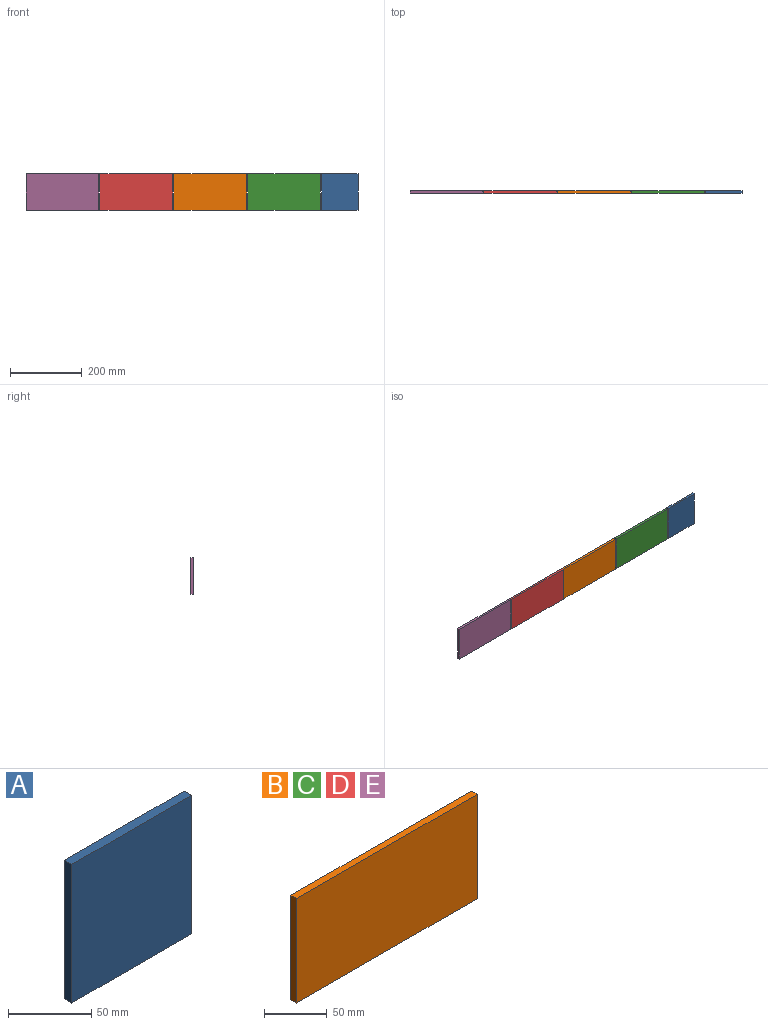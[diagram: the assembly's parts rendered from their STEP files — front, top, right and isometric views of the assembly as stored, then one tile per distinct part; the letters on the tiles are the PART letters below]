
ASSEMBLY  parts=5 mates=1
PART A: 6 faces, bbox 101.6x6.4x101.6 mm
  f0: plane 101.6x6.35mm, normal (-1,0,0), area 645.2mm2, adj f1,f3,f4,f5
  f1: plane 101.6x6.35mm, normal (0,0,-1), area 645.2mm2, adj f0,f2,f4,f5
  f2: plane 101.6x6.35mm, normal (1,0,0), area 645.2mm2, adj f1,f3,f4,f5
  f3: plane 101.6x6.35mm, normal (0,0,1), area 645.2mm2, adj f0,f2,f4,f5
  f4: plane 101.6x101.6mm, normal (0,-1,0), area 10322.6mm2, adj f0,f1,f2,f3
  f5: plane 101.6x101.6mm, normal (0,1,0), area 10322.6mm2, adj f0,f1,f2,f3
PART B: 6 faces, bbox 203.2x6.4x101.6 mm
  f0: plane 101.6x6.35mm, normal (-1,0,0), area 645.2mm2, adj f1,f3,f4,f5
  f1: plane 203.2x6.35mm, normal (0,0,-1), area 1290.3mm2, adj f0,f2,f4,f5
  f2: plane 101.6x6.35mm, normal (1,0,0), area 645.2mm2, adj f1,f3,f4,f5
  f3: plane 203.2x6.35mm, normal (0,0,1), area 1290.3mm2, adj f0,f2,f4,f5
  f4: plane 203.2x101.6mm, normal (0,-1,0), area 20645.1mm2, adj f0,f1,f2,f3
  f5: plane 203.2x101.6mm, normal (0,1,0), area 20645.1mm2, adj f0,f1,f2,f3
PART C: same geometry as B
PART D: same geometry as B
PART E: same geometry as B
PLACE A t=(593.18,0,-114.86)mm
PLACE B t=(-441.59,0,-126.88)mm
PLACE C t=(-235.22,0,-126.88)mm
PLACE D t=(-647.97,0,-126.88)mm
PLACE E t=(-854.34,0,-126.88)mm
MATE fastened A.f4 <-> C.f4  axis (0,-1,0) through (3.18,-6.35,50.8)mm
